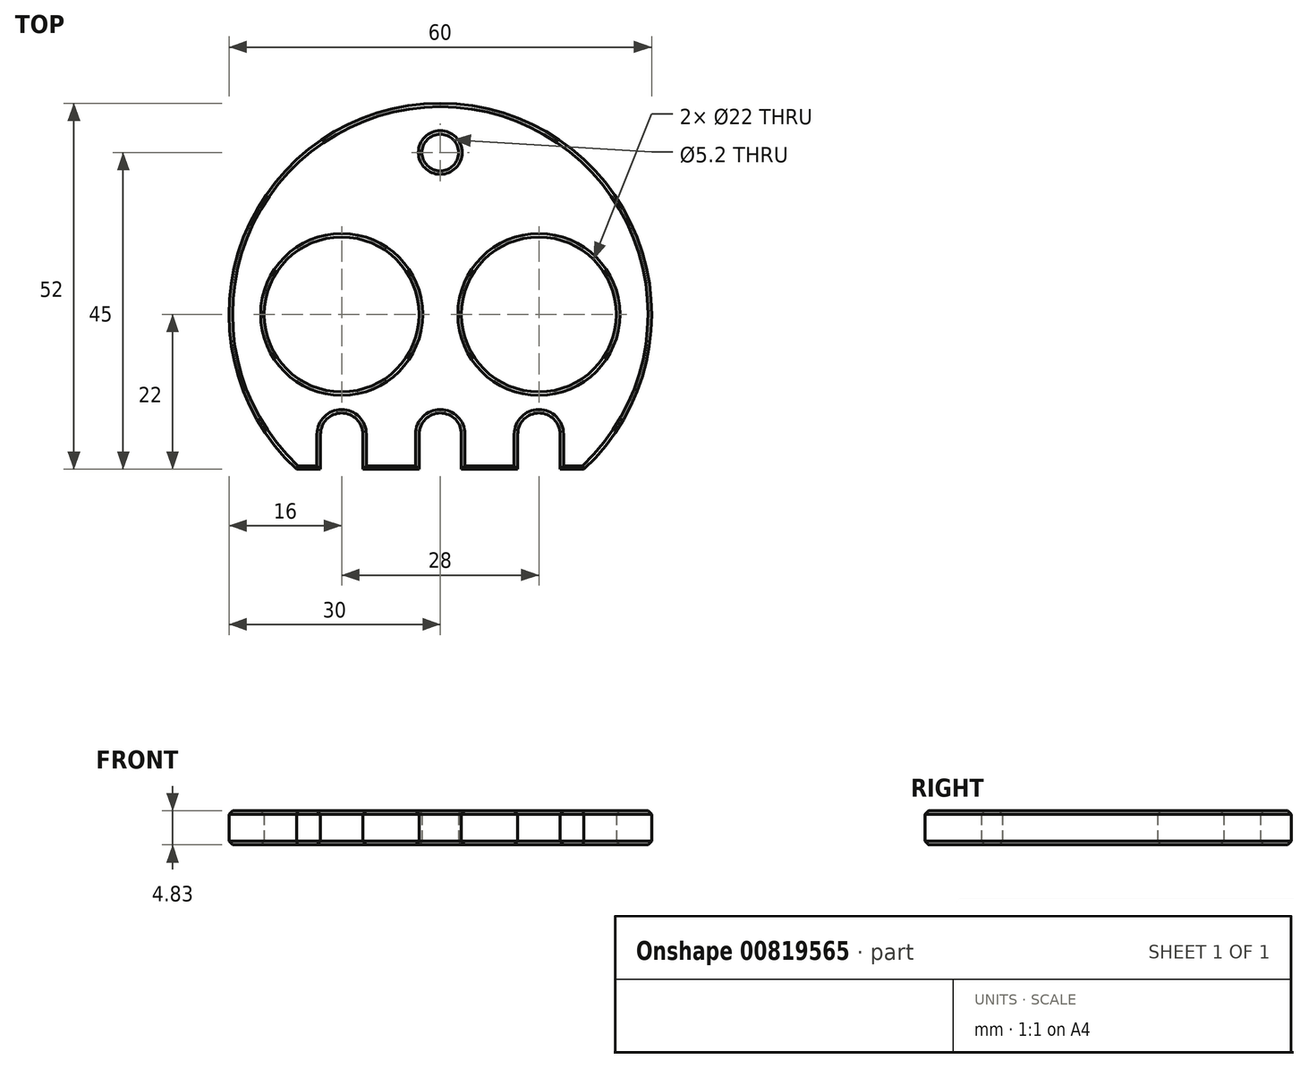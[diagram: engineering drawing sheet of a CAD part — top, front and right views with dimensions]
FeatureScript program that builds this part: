
annotation { "Feature Type Name" : "Feature", "Feature Type Description" : "" }
export const myFeature = defineFeature(function(context is Context, id is Id, definition is map)
    precondition{}
    {
        {
            var Q0;
            Q0=qCreatedBy(makeId("Top.planeOp"),FACE);
            var sketch = newSketch(context, id + "F0", { "sketchPlane" : qUnion([Q0])});
            skCircle(sketch, "E0", {"center": v(-14, 0) * mm, "radius": 11 * mm});
            skCircle(sketch, "E1", {"center": v(14, 0) * mm, "radius": 11 * mm});
            skCircle(sketch, "E2", {"center": v(0, 0) * mm, "radius": 30 * mm});
            skLineSegment(sketch, "E3", {"start": v(-42.62, -22) * mm, "end": v(52.32, -22) * mm});
            skCircle(sketch, "E4", {"center": v(0, 23) * mm, "radius": 2.6 * mm});
            skSolve(sketch);
        }
        {
            var Q0;
            Q0=makeQuery(id+"F0.imprint","IMPRINT",FACE,{"disambiguationData":[TD([[makeQuery(id+"F0.imprint","IMPRINT",EDGE,{"derivedFrom":sQuery(id+"F0.wireOp",EDGE,"E0")}),-1.0]])]});
            extrude(context, id + "F1", {"entities" : qUnion([Q0]), "depth" : 4.83 * mm, "offsetDistance" : 25 * mm});
        }
        {
            var Q0;
            Q0=makeQuery(id+"F1.opExtrude","CAP_FACE",FACE,{"disambiguationData":[OSD([sQuery(id+"F0.wireOp",EDGE,"E0"),sQuery(id+"F0.wireOp",EDGE,"E1"),sQuery(id+"F0.wireOp",EDGE,"E2"),sQuery(id+"F0.wireOp",EDGE,"E3"),sQuery(id+"F0.wireOp",EDGE,"E4")])],"isStart":true});
            var sketch = newSketch(context, id + "F2", { "sketchPlane" : qUnion([Q0])});
            skLineSegment(sketch, "E5", {"start": v(0, 22) * mm, "end": v(0, 17) * mm});
            skArc(sketch, "E6.0.startCap", {"start": v(-3, 22) * mm, "mid": v(0, 25) * mm, "end": v(3, 22) * mm});
            skArc(sketch, "E6.0.endCap", {"start": v(3, 17) * mm, "mid": v(0, 14) * mm, "end": v(-3, 17) * mm});
            skLineSegment(sketch, "E6.0.left", {"start": v(3, 22) * mm, "end": v(3, 17) * mm});
            skLineSegment(sketch, "E6.0.right", {"start": v(-3, 22) * mm, "end": v(-3, 17) * mm});
            skLineSegment(sketch, "E7.1.0.0", {"start": v(14, 22) * mm, "end": v(14, 17) * mm});
            skArc(sketch, "E7.1.0.1", {"start": v(11, 22) * mm, "mid": v(14, 25) * mm, "end": v(17, 22) * mm});
            skLineSegment(sketch, "E7.1.0.2", {"start": v(11, 22) * mm, "end": v(11, 17) * mm});
            skArc(sketch, "E7.1.0.3", {"start": v(17, 17) * mm, "mid": v(14, 14) * mm, "end": v(11, 17) * mm});
            skLineSegment(sketch, "E7.1.0.4", {"start": v(17, 22) * mm, "end": v(17, 17) * mm});
            skLineSegment(sketch, "E7.direction1", {"start": v(-3, 17) * mm, "end": v(11, 17) * mm, "construction": true});
            skLineSegment(sketch, "E8.1.0.0", {"start": v(-17, 22) * mm, "end": v(-17, 17) * mm});
            skArc(sketch, "E8.1.0.1", {"start": v(-11, 17) * mm, "mid": v(-14, 14) * mm, "end": v(-17, 17) * mm});
            skArc(sketch, "E8.1.0.2", {"start": v(-17, 22) * mm, "mid": v(-14, 25) * mm, "end": v(-11, 22) * mm});
            skLineSegment(sketch, "E8.1.0.3", {"start": v(-14, 22) * mm, "end": v(-14, 17) * mm});
            skLineSegment(sketch, "E8.1.0.4", {"start": v(-11, 22) * mm, "end": v(-11, 17) * mm});
            skLineSegment(sketch, "E8.direction1", {"start": v(-3, 17) * mm, "end": v(-17, 17) * mm, "construction": true});
            skSolve(sketch);
        }
        {
            var Q0;
            Q0 = qSketchRegion(id + "F2", true);
            extrude(context, id + "F3", {"entities" : qUnion([Q0]), "operationType" : NewBodyOperationType.REMOVE, "oppositeDirection" : true, "depth" : 25 * mm, "offsetDistance" : 25 * mm});
        }
        {
            var Q0;
            Q0=makeQuery(id+"F1.opExtrude","CAP_FACE",FACE,{"disambiguationData":[OSD([sQuery(id+"F0.wireOp",EDGE,"E0"),sQuery(id+"F0.wireOp",EDGE,"E1"),sQuery(id+"F0.wireOp",EDGE,"E2"),sQuery(id+"F0.wireOp",EDGE,"E3"),sQuery(id+"F0.wireOp",EDGE,"E4")])],"isStart":true});
            var Q1;
            Q1=makeQuery(id+"F1.opExtrude","CAP_FACE",FACE,{"disambiguationData":[OSD([sQuery(id+"F0.wireOp",EDGE,"E0"),sQuery(id+"F0.wireOp",EDGE,"E1"),sQuery(id+"F0.wireOp",EDGE,"E2"),sQuery(id+"F0.wireOp",EDGE,"E3"),sQuery(id+"F0.wireOp",EDGE,"E4")])],"isStart":false});
            chamfer(context, id + "F4", {"entities" : qUnion([Q0, Q1]), "width" : .5 * mm, "tangentPropagation" : true});
        }
    });
